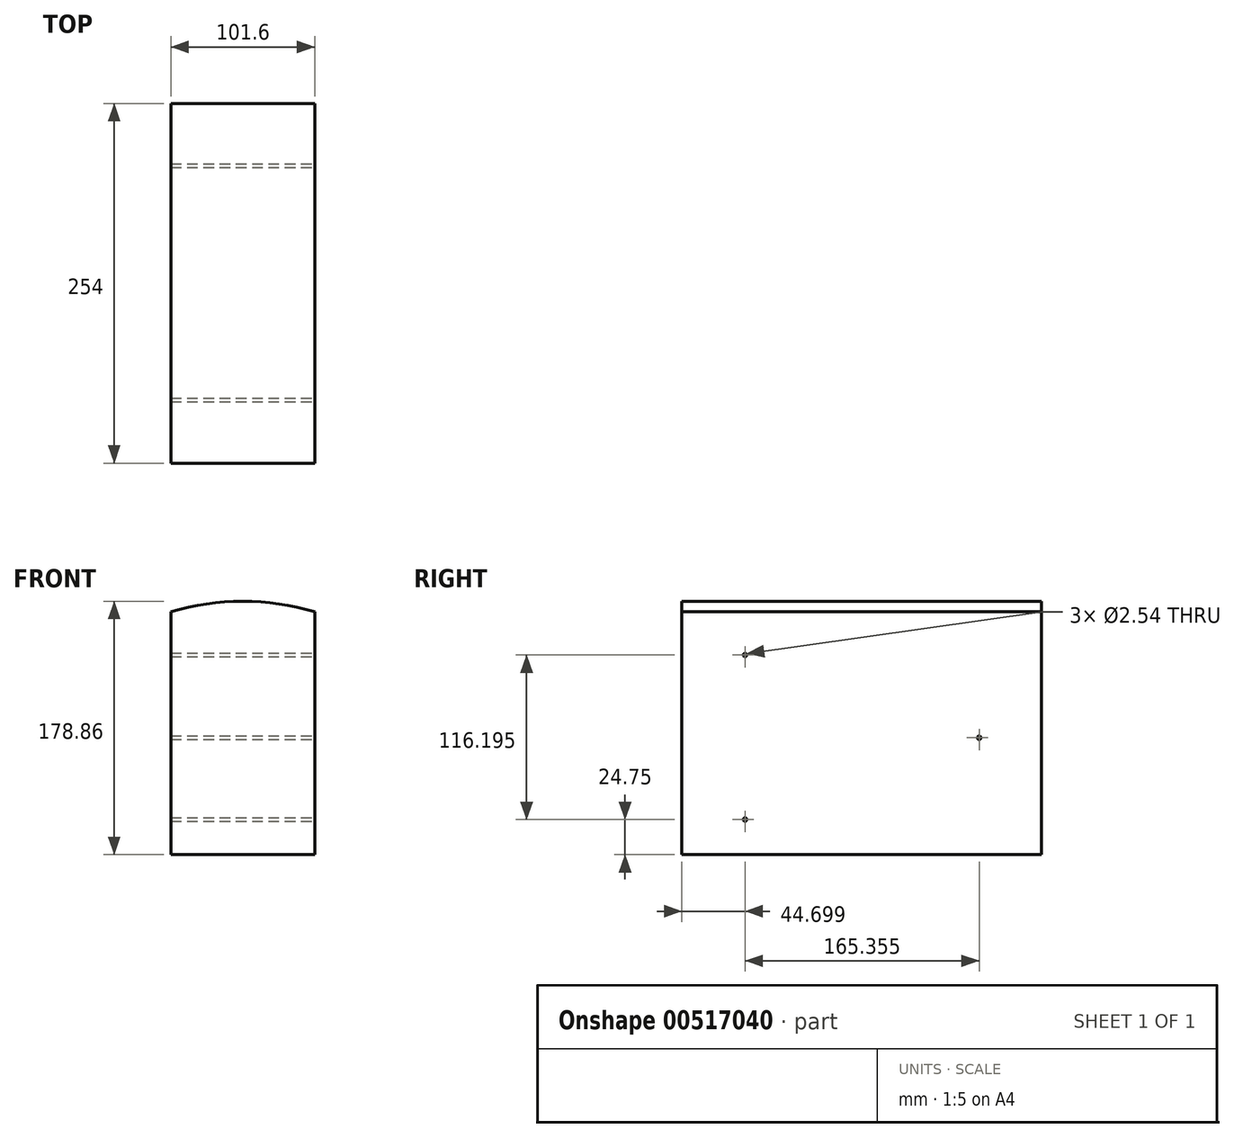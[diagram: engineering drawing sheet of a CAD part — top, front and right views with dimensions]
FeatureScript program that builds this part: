
annotation { "Feature Type Name" : "Feature", "Feature Type Description" : "" }
export const myFeature = defineFeature(function(context is Context, id is Id, definition is map)
    precondition{}
    {
        {
            var Q0;
            Q0=qCreatedBy(makeId("Front.planeOp"),FACE);
            var sketch = newSketch(context, id + "F0", { "sketchPlane" : qUnion([Q0])});
            skLineSegment(sketch, "E0.top", {"start": v(-51.18, -82.51) * mm, "end": v(50.42, -82.51) * mm});
            skLineSegment(sketch, "E0.left", {"start": v(-51.18, 88.94) * mm, "end": v(-51.18, -82.51) * mm});
            skLineSegment(sketch, "E0.right", {"start": v(50.42, 88.94) * mm, "end": v(50.42, -82.51) * mm});
            skArc(sketch, "E1", {"start": v(50.42, 88.94) * mm, "mid": v(-0.38, 96.35) * mm, "end": v(-51.18, 88.94) * mm});
            skSolve(sketch);
        }
        {
            var Q0;
            Q0=makeQuery(id+"F0.imprint","IMPRINT",FACE,{"disambiguationData":[TD([[makeQuery(id+"F0.imprint","IMPRINT",EDGE,{"derivedFrom":sQuery(id+"F0.wireOp",EDGE,"E0.top")}),1.0]])]});
            extrude(context, id + "F1", {"entities" : qUnion([Q0]), "endBound" : BoundingType.SYMMETRIC, "depth" : 254 * mm, "offsetDistance" : 25.4 * mm});
        }
        {
            var Q0;
            Q0=makeQuery(id+"F1.opExtrude","SWEPT_FACE",FACE,{"disambiguationData":[OSD([sQuery(id+"F0.wireOp",EDGE,"E0.right")])]});
            var sketch = newSketch(context, id + "F2", { "sketchPlane" : qUnion([Q0])});
            skPoint(sketch, "E2", {"position": v(-82.3, 58.44) * mm});
            skPoint(sketch, "E3", {"position": v(-82.3, -57.76) * mm});
            skPoint(sketch, "E4", {"position": v(83.05, 0) * mm});
            skSolve(sketch);
        }
        {
            var Q0;
            Q0=sQuery(id+"F2.wireOp",VERTEX,"E2");
            var Q1;
            Q1=sQuery(id+"F2.wireOp",VERTEX,"E3");
            var Q2;
            Q2=sQuery(id+"F2.wireOp",VERTEX,"E4");
            var Q3;
            Q3=makeQuery(id+"F1.opExtrude","SWEPT_BODY",BODY,{"disambiguationData":[OSD([sQuery(id+"F0.wireOp",EDGE,"E0.top"),sQuery(id+"F0.wireOp",EDGE,"E0.left"),sQuery(id+"F0.wireOp",EDGE,"E0.right"),sQuery(id+"F0.wireOp",EDGE,"E1")])]});
            hole(context, id + "F3", {"style" : HoleStyle.SIMPLE, "endStyle" : HoleEndStyle.THROUGH, "holeDiameter" : 2.54 * mm, "isTappedThrough" : true, "tappedDepth" : 12.7 * mm, "tapClearance" : 3, "locations" : qUnion([Q0, Q1, Q2]), "scope" : qUnion([Q3])});
        }
    });
